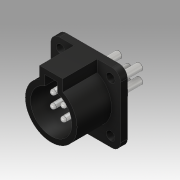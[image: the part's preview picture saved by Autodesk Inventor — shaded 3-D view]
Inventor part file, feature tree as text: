
AUTODESK INVENTOR PART (.ipt)
format: ipt  version: 2019.3 (Build 233278000, 278)  size: 235,520 bytes
history: native  units: mm
features: projected_geometry x10, extrude x5, sketch x5, fillet x1
ambient origin geometry x8: Origin, YZ Plane, XZ Plane, XY Plane, X Axis, Y Axis, Z Axis, Center Point
bodies: Solid1 (feature_tree)
feature tree (21):
  extrude  "Extrusion1"  Depth=20.2mm
  extrude  "Extrusion2"  Depth=2.5mm
  extrude  "Extrusion3"  Depth=2.5mm
  fillet  "Fillet1"  Radius=15.0mm
  extrude  "Extrusion4"  Depth=6.7mm
  extrude  "Extrusion5"  Depth=2.0mm TaperAngle=0.0deg
  sketch  "Sketch1"  dims[d0=20.2mm d1=20.2mm]
  sketch  "Sketch2"  dims[d2=2.5mm d3=17.0mm]
  projected_geometry  "Projected Loop1"
  sketch  "Sketch3"  dims[d4=17.0mm d5=2.5mm d6=15.0mm]
  sketch  "Sketch4"  dims[d7=17.6mm d8=6.7mm]
  projected_geometry  "Projected Loop2"
  projected_geometry  "Projected Loop3"
  projected_geometry  "Projected Loop4"
  projected_geometry  "Projected Loop5"
  projected_geometry  "Projected Loop6"
  sketch  "Sketch5"  dims[d9=3.35mm d10=2.0mm d11=0.0mm d12=15.0mm d13=6.7mm d14=10.1mm d15=1.5mm d16=10.0mm d17=0.0mm d18=60.0mm d20=360.0deg d22=1.5mm d23=3.5mm d24=7.0mm d25=0.0mm d26=0.75mm d27=12.5mm d28=11.0mm d29=2.0mm d30=2.5mm d31=4.0mm d32=0.0mm d33=2.0mm d34=6.5mm d35=0.0mm]
  projected_geometry  "Projected Loop7"
  projected_geometry  "Projected Loop8"
  projected_geometry  "Projected Loop9"
  projected_geometry  "Projected Loop10"
